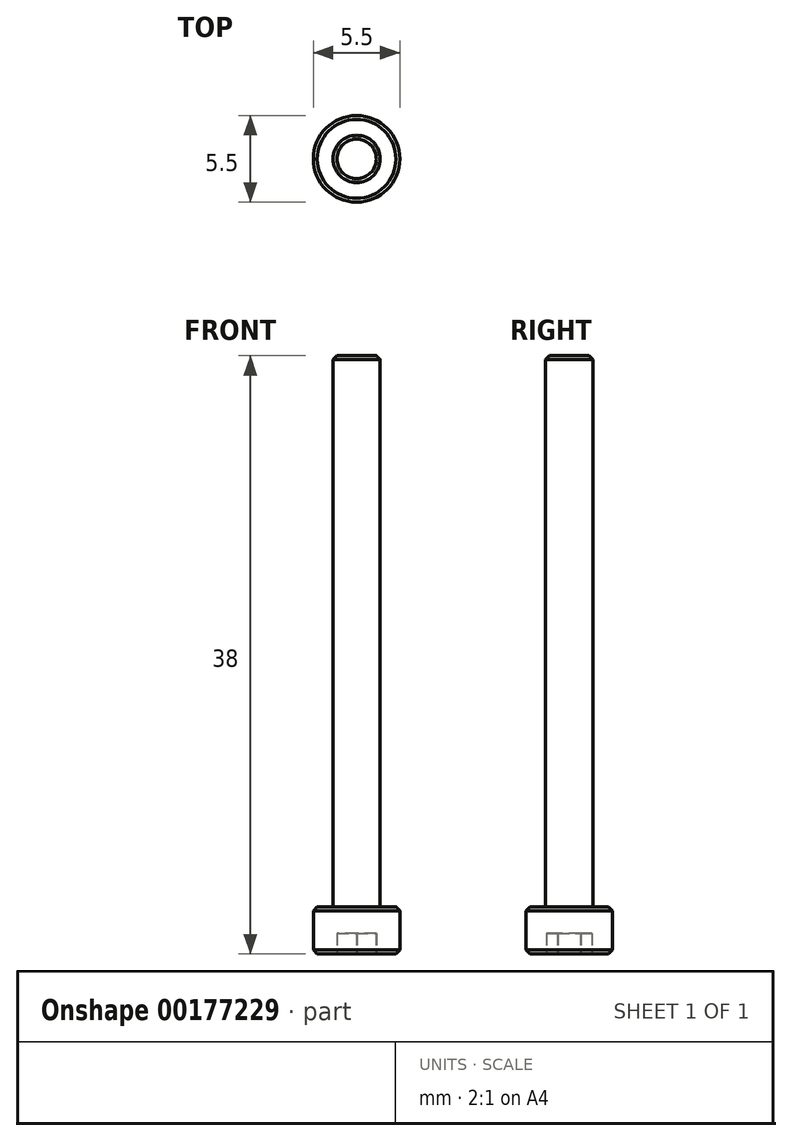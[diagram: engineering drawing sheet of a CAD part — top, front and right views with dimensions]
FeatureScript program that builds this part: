
annotation { "Feature Type Name" : "Feature", "Feature Type Description" : "" }
export const myFeature = defineFeature(function(context is Context, id is Id, definition is map)
    precondition{}
    {
        {
            var Q0;
            Q0=qCreatedBy(makeId("Top.planeOp"),FACE);
            var sketch = newSketch(context, id + "F0", { "sketchPlane" : qUnion([Q0])});
            skCircle(sketch, "E0", {"center": v(0, 0) * mm, "radius": 1.5 * mm});
            skSolve(sketch);
        }
        {
            var Q0;
            Q0=qSketchRegion(id+"F0",true);
            extrude(context, id + "F1", {"entities" : qUnion([Q0]), "depth" : 35 * mm});
        }
        {
            var Q0;
            Q0=qCreatedBy(makeId("Top.planeOp"),FACE);
            var sketch = newSketch(context, id + "F2", { "sketchPlane" : qUnion([Q0])});
            skCircle(sketch, "E1", {"center": v(0, 0) * mm, "radius": 2.75 * mm});
            skSolve(sketch);
        }
        {
            var Q0;
            Q0=qSketchRegion(id+"F2",true);
            extrude(context, id + "F3", {"entities" : qUnion([Q0]), "operationType" : NewBodyOperationType.ADD, "oppositeDirection" : true, "depth" : 3 * mm});
        }
        {
            var Q0;
            Q0=makeQuery(id+"F3.opExtrude","CAP_FACE",FACE,{"disambiguationData":[OSD([sQuery(id+"F2.wireOp",EDGE,"E1")])],"isStart":false});
            var sketch = newSketch(context, id + "F4", { "sketchPlane" : qUnion([Q0])});
            skCircle(sketch, "E2.cCircle", {"center": v(0, 0) * mm, "radius": 1.25 * mm, "construction": true});
            skLineSegment(sketch, "E2.0", {"start": v(1.26, -0.7) * mm, "end": v(0.02, -1.44) * mm});
            skLineSegment(sketch, "E2.1", {"start": v(0.02, -1.44) * mm, "end": v(-1.24, -0.74) * mm});
            skLineSegment(sketch, "E2.2", {"start": v(-1.24, -0.74) * mm, "end": v(-1.26, 0.7) * mm});
            skLineSegment(sketch, "E2.3", {"start": v(-1.26, 0.7) * mm, "end": v(-0.02, 1.44) * mm});
            skLineSegment(sketch, "E2.4", {"start": v(-0.02, 1.44) * mm, "end": v(1.24, 0.74) * mm});
            skLineSegment(sketch, "E2.5", {"start": v(1.24, 0.74) * mm, "end": v(1.26, -0.7) * mm});
            skPoint(sketch, "E2.0.midPoint", {"position": v(0.64, -1.07) * mm});
            skSolve(sketch);
        }
        {
            var Q0;
            Q0=qSketchRegion(id+"F4",true);
            extrude(context, id + "F5", {"entities" : qUnion([Q0]), "operationType" : NewBodyOperationType.REMOVE, "oppositeDirection" : true, "depth" : 1.3 * mm});
        }
        {
            var Q0;
            Q0=makeQuery(id+"F3.opExtrude","CAP_EDGE",EDGE,{"disambiguationData":[OSD([sQuery(id+"F2.wireOp",EDGE,"E1")])],"isStart":false});
            var Q1;
            Q1=makeQuery(id+"F3.opExtrude","CAP_EDGE",EDGE,{"disambiguationData":[OSD([sQuery(id+"F2.wireOp",EDGE,"E1")])],"isStart":true});
            var Q2;
            Q2=makeQuery(id+"F1.opExtrude","CAP_EDGE",EDGE,{"disambiguationData":[OSD([sQuery(id+"F0.wireOp",EDGE,"E0")])],"isStart":false});
            chamfer(context, id + "F6", {"entities" : qUnion([Q0, Q1, Q2]), "width" : .25 * mm, "tangentPropagation" : true});
        }
    });
